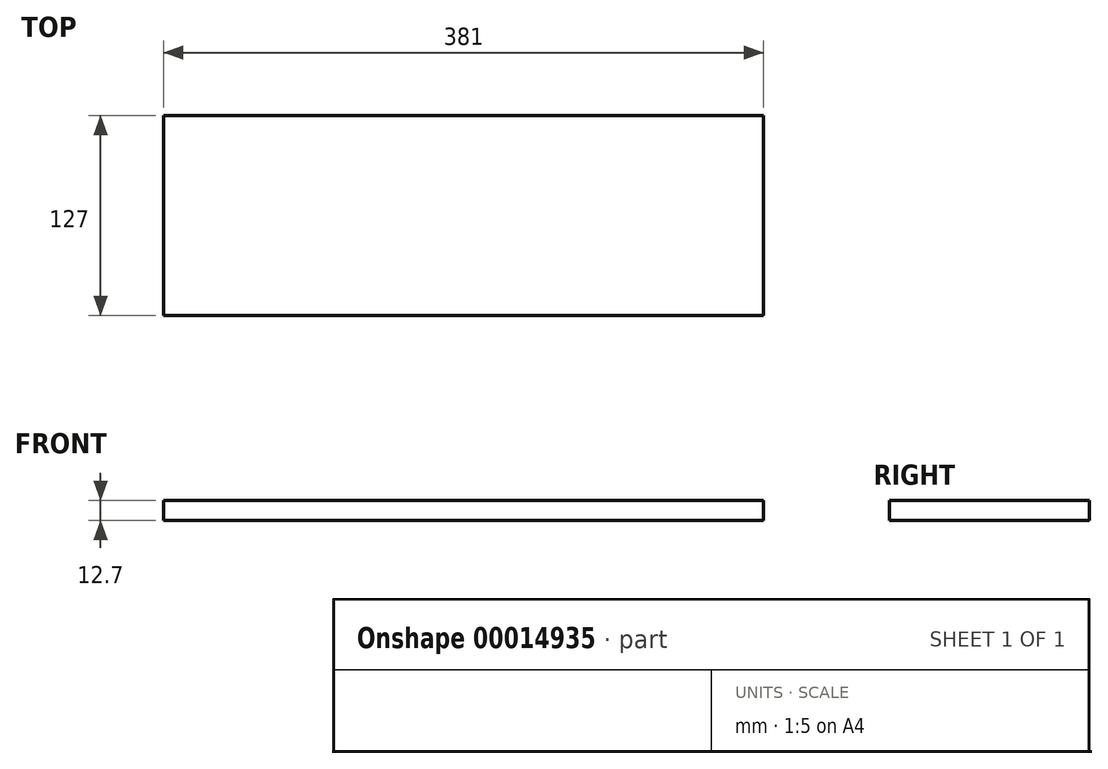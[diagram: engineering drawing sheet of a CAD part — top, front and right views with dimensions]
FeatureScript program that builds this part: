
annotation { "Feature Type Name" : "Feature", "Feature Type Description" : "" }
export const myFeature = defineFeature(function(context is Context, id is Id, definition is map)
    precondition{}
    {
        {
            var Q0;
            Q0=qCreatedBy(makeId("Top.planeOp"),FACE);
            var sketch = newSketch(context, id + "F0", { "sketchPlane" : qUnion([Q0])});
            skLineSegment(sketch, "E0.bottom", {"start": v(-173.24, 27.4) * mm, "end": v(207.76, 27.4) * mm});
            skLineSegment(sketch, "E0.top", {"start": v(-173.24, -99.6) * mm, "end": v(207.76, -99.6) * mm});
            skLineSegment(sketch, "E0.left", {"start": v(-173.24, 27.4) * mm, "end": v(-173.24, -99.6) * mm});
            skLineSegment(sketch, "E0.right", {"start": v(207.76, 27.4) * mm, "end": v(207.76, -99.6) * mm});
            skSolve(sketch);
        }
        {
            var Q0;
            Q0=makeQuery(id+"F0.imprint","IMPRINT",FACE,{"disambiguationData":[TD([[makeQuery(id+"F0.imprint","IMPRINT",EDGE,{"derivedFrom":sQuery(id+"F0.wireOp",EDGE,"E0.bottom")}),-1.0]])]});
            extrude(context, id + "F1", {"entities" : qUnion([Q0]), "depth" : 12.7 * mm});
        }
    });
